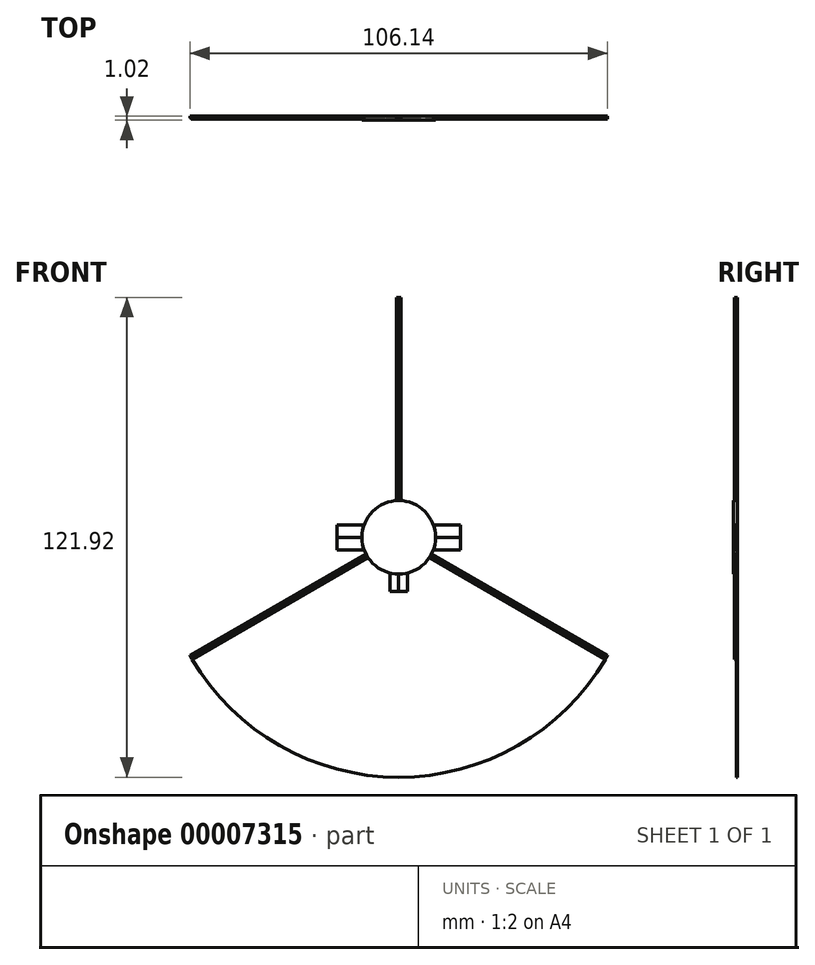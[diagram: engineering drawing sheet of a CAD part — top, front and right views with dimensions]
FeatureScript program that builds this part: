
annotation { "Feature Type Name" : "Feature", "Feature Type Description" : "" }
export const myFeature = defineFeature(function(context is Context, id is Id, definition is map)
    precondition{}
    {
        {
            var Q0;
            Q0=qCreatedBy(makeId("Front.planeOp"),FACE);
            var sketch = newSketch(context, id + "F0", { "sketchPlane" : qUnion([Q0])});
            skCircle(sketch, "E0", {"center": v(0, 0) * mm, "radius": 60.96 * mm});
            skCircle(sketch, "E1", {"center": v(0, 0) * mm, "radius": 9.35 * mm});
            skLineSegment(sketch, "E2", {"start": v(0, 0) * mm, "end": v(0, 60.96) * mm});
            skLineSegment(sketch, "E3", {"start": v(0, 0) * mm, "end": v(52.8, -30.48) * mm});
            skLineSegment(sketch, "E4", {"start": v(0, 0) * mm, "end": v(-52.8, -30.48) * mm});
            skLineSegment(sketch, "E5", {"start": v(0, 0) * mm, "end": v(0.57, 0) * mm});
            skLineSegment(sketch, "E6", {"start": v(0.57, 0) * mm, "end": v(0.57, 60.96) * mm});
            skLineSegment(sketch, "E7.MirrorCS", {"start": v(-0.57, 0) * mm, "end": v(-0.57, 60.96) * mm});
            skLineSegment(sketch, "E8.MirrorCS", {"start": v(0, 0) * mm, "end": v(-0.57, 0) * mm});
            skLineSegment(sketch, "E9", {"start": v(0, 0) * mm, "end": v(-0.28, -0.49) * mm});
            skLineSegment(sketch, "E10", {"start": v(-0.28, -0.49) * mm, "end": v(52.5, -30.97) * mm});
            skLineSegment(sketch, "E11.MirrorCS", {"start": v(0.28, 0.49) * mm, "end": v(53.07, -29.99) * mm});
            skLineSegment(sketch, "E12.MirrorCS", {"start": v(0, 0) * mm, "end": v(0.28, 0.49) * mm});
            skLineSegment(sketch, "E13.MirrorCS", {"start": v(-0.28, 0.49) * mm, "end": v(-53.07, -29.99) * mm});
            skLineSegment(sketch, "E14.MirrorCS", {"start": v(0, 0) * mm, "end": v(-0.28, 0.49) * mm});
            skLineSegment(sketch, "E15.MirrorCS", {"start": v(0, 0) * mm, "end": v(0.28, -0.49) * mm});
            skLineSegment(sketch, "E16.MirrorCS", {"start": v(0.28, -0.49) * mm, "end": v(-52.5, -30.97) * mm});
            skLineSegment(sketch, "E17", {"start": v(0, 0) * mm, "end": v(0, -9.35) * mm});
            skLineSegment(sketch, "E18", {"start": v(0, -9.35) * mm, "end": v(0, -60.96) * mm});
            skCircle(sketch, "E19", {"center": v(0, -11.52) * mm, "radius": 2.17 * mm});
            skLineSegment(sketch, "E20", {"start": v(-2.17, -13.7) * mm, "end": v(0, -13.7) * mm});
            skLineSegment(sketch, "E21", {"start": v(0, -13.7) * mm, "end": v(2.17, -13.7) * mm});
            skLineSegment(sketch, "E22", {"start": v(2.17, -13.7) * mm, "end": v(2.17, -9.1) * mm});
            skLineSegment(sketch, "E23", {"start": v(-2.17, -9.1) * mm, "end": v(-2.17, -13.7) * mm});
            skLineSegment(sketch, "E24", {"start": v(-8.8, 3.17) * mm, "end": v(-15.7, 3.17) * mm});
            skLineSegment(sketch, "E25", {"start": v(-15.7, 3.17) * mm, "end": v(-15.7, 0) * mm});
            skLineSegment(sketch, "E26", {"start": v(-15.7, 0) * mm, "end": v(-15.7, -3.18) * mm});
            skLineSegment(sketch, "E27", {"start": v(-15.7, -3.18) * mm, "end": v(-8.8, -3.18) * mm});
            skLineSegment(sketch, "E28", {"start": v(-15.7, 0) * mm, "end": v(0, 0) * mm});
            skLineSegment(sketch, "E29.MirrorCS", {"start": v(8.8, 3.17) * mm, "end": v(15.7, 3.17) * mm});
            skLineSegment(sketch, "E30.MirrorCS", {"start": v(15.7, 0) * mm, "end": v(0, 0) * mm});
            skLineSegment(sketch, "E31.MirrorCS", {"start": v(15.7, 3.17) * mm, "end": v(15.7, 0) * mm});
            skLineSegment(sketch, "E32.MirrorCS", {"start": v(15.7, 0) * mm, "end": v(15.7, -3.18) * mm});
            skLineSegment(sketch, "E33.MirrorCS", {"start": v(15.7, -3.18) * mm, "end": v(8.8, -3.18) * mm});
            skSolve(sketch);
        }
        {
            var Q0;
            {var subQ3=sQuery(id+"F0.wireOp",EDGE,"E20");Q0=makeQuery(id+"F0.imprint","IMPRINT",FACE,{"disambiguationData":[TD([[makeQuery(id+"F0.imprint","IMPRINT",EDGE,{"derivedFrom":subQ3}),-1.0]])]});}
            var Q1;
            {var subQ7=sQuery(id+"F0.wireOp",EDGE,"E21");Q1=makeQuery(id+"F0.imprint","IMPRINT",FACE,{"disambiguationData":[TD([[makeQuery(id+"F0.imprint","IMPRINT",EDGE,{"derivedFrom":subQ7}),-1.0]])]});}
            var Q2;
            {var subQ8=sQuery(id+"F0.wireOp",EDGE,"E29.MirrorCS");Q2=makeQuery(id+"F0.imprint","IMPRINT",FACE,{"disambiguationData":[TD([[makeQuery(id+"F0.imprint","IMPRINT",EDGE,{"derivedFrom":subQ8}),1.0]])]});}
            var Q3;
            {var subQ8=sQuery(id+"F0.wireOp",EDGE,"E24");Q3=makeQuery(id+"F0.imprint","IMPRINT",FACE,{"disambiguationData":[TD([[makeQuery(id+"F0.imprint","IMPRINT",EDGE,{"derivedFrom":subQ8}),-1.0]])]});}
            extrude(context, id + "F1", {"entities" : qUnion([Q0, Q1, Q2, Q3]), "depth" : 0.25 * mm});
        }
        {
            var Q0;
            {var subQ0=sQuery(id+"F0.wireOp",EDGE,"E4");var subQ1=sQuery(id+"F0.wireOp",EDGE,"E0");var subQ2=makeQuery(id+"F0.imprint","INTERSECT",VERTEX,{"derivedFrom":[subQ1,subQ0]});Q0=makeQuery(id+"F0.imprint","IMPRINT",FACE,{"disambiguationData":[TD([[makeQuery(id+"F0.imprint","IMPRINT",EDGE,{"disambiguationData":[TD([[subQ2,1.0]])],"derivedFrom":subQ1}),1.0]])]});}
            var Q1;
            {var subQ0=sQuery(id+"F0.wireOp",EDGE,"E2");var subQ1=sQuery(id+"F0.wireOp",EDGE,"E0");var subQ2=makeQuery(id+"F0.imprint","INTERSECT",VERTEX,{"derivedFrom":[subQ1,subQ0]});Q1=makeQuery(id+"F0.imprint","IMPRINT",FACE,{"disambiguationData":[TD([[makeQuery(id+"F0.imprint","IMPRINT",EDGE,{"disambiguationData":[TD([[subQ2,1.0]])],"derivedFrom":subQ1}),1.0]])]});}
            var Q2;
            {var subQ0=sQuery(id+"F0.wireOp",EDGE,"E3");var subQ1=sQuery(id+"F0.wireOp",EDGE,"E0");var subQ2=makeQuery(id+"F0.imprint","INTERSECT",VERTEX,{"derivedFrom":[subQ1,subQ0]});Q2=makeQuery(id+"F0.imprint","IMPRINT",FACE,{"disambiguationData":[TD([[makeQuery(id+"F0.imprint","IMPRINT",EDGE,{"disambiguationData":[TD([[subQ2,1.0]])],"derivedFrom":subQ1}),1.0]])]});}
            extrude(context, id + "F2", {"entities" : qUnion([Q0, Q1, Q2]), "operationType" : NewBodyOperationType.ADD, "depth" : 0.5 * mm});
        }
        {
            var Q0;
            {var subQ0=sQuery(id+"F0.wireOp",EDGE,"E4");var subQ1=sQuery(id+"F0.wireOp",EDGE,"E0");var subQ2=makeQuery(id+"F0.imprint","INTERSECT",VERTEX,{"derivedFrom":[subQ1,subQ0]});Q0=makeQuery(id+"F0.imprint","IMPRINT",FACE,{"disambiguationData":[TD([[makeQuery(id+"F0.imprint","IMPRINT",EDGE,{"disambiguationData":[TD([[subQ2,-1.0]])],"derivedFrom":subQ1}),1.0]])]});}
            var Q1;
            {var subQ0=sQuery(id+"F0.wireOp",EDGE,"E2");var subQ1=sQuery(id+"F0.wireOp",EDGE,"E0");var subQ2=makeQuery(id+"F0.imprint","INTERSECT",VERTEX,{"derivedFrom":[subQ1,subQ0]});Q1=makeQuery(id+"F0.imprint","IMPRINT",FACE,{"disambiguationData":[TD([[makeQuery(id+"F0.imprint","IMPRINT",EDGE,{"disambiguationData":[TD([[subQ2,-1.0]])],"derivedFrom":subQ1}),1.0]])]});}
            var Q2;
            {var subQ0=sQuery(id+"F0.wireOp",EDGE,"E3");var subQ1=sQuery(id+"F0.wireOp",EDGE,"E0");var subQ2=makeQuery(id+"F0.imprint","INTERSECT",VERTEX,{"derivedFrom":[subQ1,subQ0]});Q2=makeQuery(id+"F0.imprint","IMPRINT",FACE,{"disambiguationData":[TD([[makeQuery(id+"F0.imprint","IMPRINT",EDGE,{"disambiguationData":[TD([[subQ2,-1.0]])],"derivedFrom":subQ1}),1.0]])]});}
            extrude(context, id + "F3", {"entities" : qUnion([Q0, Q1, Q2]), "operationType" : NewBodyOperationType.ADD, "depth" : 0.76 * mm});
        }
        {
            var Q0;
            {var subQ4=sQuery(id+"F0.wireOp",EDGE,"E26");Q0=makeQuery(id+"F0.imprint","IMPRINT",FACE,{"disambiguationData":[TD([[makeQuery(id+"F0.imprint","IMPRINT",EDGE,{"derivedFrom":subQ4}),1.0]])]});}
            var Q1;
            {var subQ0=sQuery(id+"F0.wireOp",EDGE,"E29.MirrorCS");Q1=makeQuery(id+"F0.imprint","IMPRINT",FACE,{"disambiguationData":[TD([[makeQuery(id+"F0.imprint","IMPRINT",EDGE,{"derivedFrom":subQ0}),-1.0]])]});}
            extrude(context, id + "F4", {"entities" : qUnion([Q0, Q1]), "operationType" : NewBodyOperationType.ADD, "depth" : 0.5 * mm});
        }
        {
            var Q0;
            {var subQ0=sQuery(id+"F0.wireOp",EDGE,"E24");Q0=makeQuery(id+"F0.imprint","IMPRINT",FACE,{"disambiguationData":[TD([[makeQuery(id+"F0.imprint","IMPRINT",EDGE,{"derivedFrom":subQ0}),1.0]])]});}
            var Q1;
            {var subQ4=sQuery(id+"F0.wireOp",EDGE,"E32.MirrorCS");Q1=makeQuery(id+"F0.imprint","IMPRINT",FACE,{"disambiguationData":[TD([[makeQuery(id+"F0.imprint","IMPRINT",EDGE,{"derivedFrom":subQ4}),-1.0]])]});}
            extrude(context, id + "F5", {"entities" : qUnion([Q0, Q1]), "operationType" : NewBodyOperationType.ADD, "depth" : 0.76 * mm});
        }
        {
            var Q0;
            {var subQ1=sQuery(id+"F0.wireOp",EDGE,"E1");var subQ7=makeQuery(id+"F0.imprint","INTERSECT",VERTEX,{"derivedFrom":[subQ1,sQuery(id+"F0.wireOp",EDGE,"E24")]});Q0=makeQuery(id+"F0.imprint","IMPRINT",FACE,{"disambiguationData":[TD([[makeQuery(id+"F0.imprint","IMPRINT",EDGE,{"disambiguationData":[TD([[subQ7,1.0]])],"derivedFrom":subQ1}),1.0]])]});}
            var Q1;
            {var subQ0=sQuery(id+"F0.wireOp",EDGE,"E14.MirrorCS");Q1=makeQuery(id+"F0.imprint","IMPRINT",FACE,{"disambiguationData":[TD([[makeQuery(id+"F0.imprint","IMPRINT",EDGE,{"derivedFrom":subQ0}),-1.0]])]});}
            var Q2;
            {var subQ0=sQuery(id+"F0.wireOp",EDGE,"E12.MirrorCS");Q2=makeQuery(id+"F0.imprint","IMPRINT",FACE,{"disambiguationData":[TD([[makeQuery(id+"F0.imprint","IMPRINT",EDGE,{"derivedFrom":subQ0}),1.0]])]});}
            var Q3;
            {var subQ0=sQuery(id+"F0.wireOp",EDGE,"E1");var subQ1=makeQuery(id+"F0.imprint","INTERSECT",VERTEX,{"derivedFrom":[subQ0,sQuery(id+"F0.wireOp",EDGE,"E29.MirrorCS")]});Q3=makeQuery(id+"F0.imprint","IMPRINT",FACE,{"disambiguationData":[TD([[makeQuery(id+"F0.imprint","IMPRINT",EDGE,{"disambiguationData":[TD([[subQ1,1.0]])],"derivedFrom":subQ0}),1.0]])]});}
            var Q4;
            {var subQ0=sQuery(id+"F0.wireOp",EDGE,"E28");var subQ1=sQuery(id+"F0.wireOp",EDGE,"E7.MirrorCS");var subQ2=makeQuery(id+"F0.imprint","INTERSECT",VERTEX,{"derivedFrom":[subQ1,subQ0]});Q4=makeQuery(id+"F0.imprint","IMPRINT",FACE,{"disambiguationData":[TD([[makeQuery(id+"F0.imprint","IMPRINT",EDGE,{"disambiguationData":[TD([[subQ2,-1.0]])],"derivedFrom":subQ1}),1.0]])]});}
            var Q5;
            {var subQ5=sQuery(id+"F0.wireOp",EDGE,"E14.MirrorCS");Q5=makeQuery(id+"F0.imprint","IMPRINT",FACE,{"disambiguationData":[TD([[makeQuery(id+"F0.imprint","IMPRINT",EDGE,{"derivedFrom":subQ5}),1.0]])]});}
            var Q6;
            {var subQ5=sQuery(id+"F0.wireOp",EDGE,"E12.MirrorCS");Q6=makeQuery(id+"F0.imprint","IMPRINT",FACE,{"disambiguationData":[TD([[makeQuery(id+"F0.imprint","IMPRINT",EDGE,{"derivedFrom":subQ5}),-1.0]])]});}
            var Q7;
            {var subQ0=sQuery(id+"F0.wireOp",EDGE,"E30.MirrorCS");var subQ1=sQuery(id+"F0.wireOp",EDGE,"E6");var subQ2=makeQuery(id+"F0.imprint","INTERSECT",VERTEX,{"derivedFrom":[subQ1,subQ0]});Q7=makeQuery(id+"F0.imprint","IMPRINT",FACE,{"disambiguationData":[TD([[makeQuery(id+"F0.imprint","IMPRINT",EDGE,{"disambiguationData":[TD([[subQ2,-1.0]])],"derivedFrom":subQ1}),-1.0]])]});}
            var Q8;
            {var subQ0=sQuery(id+"F0.wireOp",EDGE,"E1");var subQ1=makeQuery(id+"F0.imprint","INTERSECT",VERTEX,{"derivedFrom":[subQ0,sQuery(id+"F0.wireOp",EDGE,"E33.MirrorCS")]});Q8=makeQuery(id+"F0.imprint","IMPRINT",FACE,{"disambiguationData":[TD([[makeQuery(id+"F0.imprint","IMPRINT",EDGE,{"disambiguationData":[TD([[subQ1,1.0]])],"derivedFrom":subQ0}),1.0]])]});}
            var Q9;
            {var subQ0=sQuery(id+"F0.wireOp",EDGE,"E1");var subQ1=makeQuery(id+"F0.imprint","INTERSECT",VERTEX,{"derivedFrom":[subQ0,sQuery(id+"F0.wireOp",EDGE,"E27")]});Q9=makeQuery(id+"F0.imprint","IMPRINT",FACE,{"disambiguationData":[TD([[makeQuery(id+"F0.imprint","IMPRINT",EDGE,{"disambiguationData":[TD([[subQ1,1.0]])],"derivedFrom":subQ0}),1.0]])]});}
            var Q10;
            {var subQ0=sQuery(id+"F0.wireOp",EDGE,"E13.MirrorCS");var subQ1=sQuery(id+"F0.wireOp",EDGE,"E1");var subQ2=makeQuery(id+"F0.imprint","INTERSECT",VERTEX,{"derivedFrom":[subQ1,subQ0]});Q10=makeQuery(id+"F0.imprint","IMPRINT",FACE,{"disambiguationData":[TD([[makeQuery(id+"F0.imprint","IMPRINT",EDGE,{"disambiguationData":[TD([[subQ2,-1.0]])],"derivedFrom":subQ1}),1.0]])]});}
            var Q11;
            {var subQ0=sQuery(id+"F0.wireOp",EDGE,"E1");var subQ1=makeQuery(id+"F0.imprint","INTERSECT",VERTEX,{"derivedFrom":[subQ0,sQuery(id+"F0.wireOp",EDGE,"E23")]});Q11=makeQuery(id+"F0.imprint","IMPRINT",FACE,{"disambiguationData":[TD([[makeQuery(id+"F0.imprint","IMPRINT",EDGE,{"disambiguationData":[TD([[subQ1,1.0]])],"derivedFrom":subQ0}),1.0]])]});}
            var Q12;
            {var subQ1=sQuery(id+"F0.wireOp",EDGE,"E1");var subQ3=makeQuery(id+"F0.imprint","INTERSECT",VERTEX,{"derivedFrom":[subQ1,sQuery(id+"F0.wireOp",EDGE,"E22")]});Q12=makeQuery(id+"F0.imprint","IMPRINT",FACE,{"disambiguationData":[TD([[makeQuery(id+"F0.imprint","IMPRINT",EDGE,{"disambiguationData":[TD([[subQ3,-1.0]])],"derivedFrom":subQ1}),1.0]])]});}
            var Q13;
            {var subQ6=sQuery(id+"F0.wireOp",EDGE,"E15.MirrorCS");Q13=makeQuery(id+"F0.imprint","IMPRINT",FACE,{"disambiguationData":[TD([[makeQuery(id+"F0.imprint","IMPRINT",EDGE,{"derivedFrom":subQ6}),1.0]])]});}
            var Q14;
            {var subQ4=sQuery(id+"F0.wireOp",EDGE,"E1");var subQ6=sQuery(id+"F0.wireOp",EDGE,"E3");var subQ8=makeQuery(id+"F0.imprint","INTERSECT",VERTEX,{"derivedFrom":[subQ4,subQ6]});Q14=makeQuery(id+"F0.imprint","IMPRINT",FACE,{"disambiguationData":[TD([[makeQuery(id+"F0.imprint","IMPRINT",EDGE,{"disambiguationData":[TD([[subQ8,-1.0]])],"derivedFrom":subQ4}),1.0]])]});}
            var Q15;
            {var subQ1=sQuery(id+"F0.wireOp",EDGE,"E9");Q15=makeQuery(id+"F0.imprint","IMPRINT",FACE,{"disambiguationData":[TD([[makeQuery(id+"F0.imprint","IMPRINT",EDGE,{"derivedFrom":subQ1}),-1.0]])]});}
            var Q16;
            {var subQ0=sQuery(id+"F0.wireOp",EDGE,"E15.MirrorCS");Q16=makeQuery(id+"F0.imprint","IMPRINT",FACE,{"disambiguationData":[TD([[makeQuery(id+"F0.imprint","IMPRINT",EDGE,{"derivedFrom":subQ0}),-1.0]])]});}
            var Q17;
            {var subQ0=sQuery(id+"F0.wireOp",EDGE,"E9");Q17=makeQuery(id+"F0.imprint","IMPRINT",FACE,{"disambiguationData":[TD([[makeQuery(id+"F0.imprint","IMPRINT",EDGE,{"derivedFrom":subQ0}),1.0]])]});}
            extrude(context, id + "F6", {"entities" : qUnion([Q0, Q1, Q2, Q3, Q4, Q5, Q6, Q7, Q8, Q9, Q10, Q11, Q12, Q13, Q14, Q15, Q16, Q17]), "operationType" : NewBodyOperationType.ADD, "depth" : 1.02 * mm});
        }
        {
            var Q0;
            {var subQ1=sQuery(id+"F0.wireOp",EDGE,"E1");var subQ3=sQuery(id+"F0.wireOp",EDGE,"E22");var subQ4=makeQuery(id+"F0.imprint","INTERSECT",VERTEX,{"derivedFrom":[subQ1,subQ3]});Q0=makeQuery(id+"F0.imprint","IMPRINT",FACE,{"disambiguationData":[TD([[makeQuery(id+"F0.imprint","IMPRINT",EDGE,{"disambiguationData":[TD([[subQ4,1.0]])],"derivedFrom":subQ3}),1.0]])]});}
            var Q1;
            {var subQ0=sQuery(id+"F0.wireOp",EDGE,"E19");var subQ4=makeQuery(id+"F0.imprint","INTERSECT",VERTEX,{"derivedFrom":[subQ0,sQuery(id+"F0.wireOp",EDGE,"E22")]});Q1=makeQuery(id+"F0.imprint","IMPRINT",FACE,{"disambiguationData":[TD([[makeQuery(id+"F0.imprint","IMPRINT",EDGE,{"disambiguationData":[TD([[subQ4,-1.0]])],"derivedFrom":subQ0}),1.0]])]});}
            var Q2;
            {var subQ0=sQuery(id+"F0.wireOp",EDGE,"E21");Q2=makeQuery(id+"F0.imprint","IMPRINT",FACE,{"disambiguationData":[TD([[makeQuery(id+"F0.imprint","IMPRINT",EDGE,{"derivedFrom":subQ0}),1.0]])]});}
            extrude(context, id + "F7", {"entities" : qUnion([Q0, Q1, Q2]), "operationType" : NewBodyOperationType.ADD, "depth" : 0.5 * mm});
        }
        {
            var Q0;
            {var subQ1=sQuery(id+"F0.wireOp",EDGE,"E1");var subQ3=sQuery(id+"F0.wireOp",EDGE,"E23");var subQ4=makeQuery(id+"F0.imprint","INTERSECT",VERTEX,{"derivedFrom":[subQ1,subQ3]});Q0=makeQuery(id+"F0.imprint","IMPRINT",FACE,{"disambiguationData":[TD([[makeQuery(id+"F0.imprint","IMPRINT",EDGE,{"disambiguationData":[TD([[subQ4,-1.0]])],"derivedFrom":subQ3}),1.0]])]});}
            var Q1;
            {var subQ0=sQuery(id+"F0.wireOp",EDGE,"E19");var subQ4=makeQuery(id+"F0.imprint","INTERSECT",VERTEX,{"derivedFrom":[subQ0,sQuery(id+"F0.wireOp",EDGE,"E23")]});Q1=makeQuery(id+"F0.imprint","IMPRINT",FACE,{"disambiguationData":[TD([[makeQuery(id+"F0.imprint","IMPRINT",EDGE,{"disambiguationData":[TD([[subQ4,1.0]])],"derivedFrom":subQ0}),1.0]])]});}
            var Q2;
            {var subQ0=sQuery(id+"F0.wireOp",EDGE,"E20");Q2=makeQuery(id+"F0.imprint","IMPRINT",FACE,{"disambiguationData":[TD([[makeQuery(id+"F0.imprint","IMPRINT",EDGE,{"derivedFrom":subQ0}),1.0]])]});}
            extrude(context, id + "F8", {"entities" : qUnion([Q0, Q1, Q2]), "operationType" : NewBodyOperationType.ADD, "depth" : 0.76 * mm});
        }
    });
